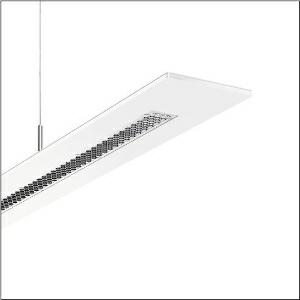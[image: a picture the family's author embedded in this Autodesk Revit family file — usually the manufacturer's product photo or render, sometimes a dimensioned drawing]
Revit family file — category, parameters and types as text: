
# Revit family: arktika_r__21_5mb2512l30840_559e
name_source: partatom
category: Lighting Fixtures
units: mm (PartAtom-declared; Revit-internal decimal feet)

## family parameters
Cut with Voids When Loaded = No
Host = Face
Light Source = No
Part Type = Normal
Room Calculation Point = No
Round Connector Dimension = Use Diameter
Shared = No

## types (1)
- Arktika® 21 (1 x LED 4000K / CRI = 80 (unbekannt), 4000 lm, 4000K)
    Apparent Load = 31 VA
    CIE Flux Codes = 81 100 100 79 100
    Color Rendering = 80
    Color Temperature = 4000K
    Default Elevation = 1800 mm
    Description = Arktika® 21, office luminaire, primary anti-glare with honeycomb louvre, of plastic, aluminium vaporised, highly specular, light emission: direct/indirect distribution, primary light characteristic: symmetric, installation type: suspended mounting, LED, rated luminous flux: 4.000lm, luminous efficacy: 130lm/W, light colour: 840, colour temperature: 4000K, control gear: ON/OFF, with terminal, 3-pole, mains connection: 220..240V, AC, 50/60Hz, rated input power: 31W, housing, of aluminium, powder-coated, traffic white (RAL 9016), 1-length, length: 1.250mm, width: 120mm, height: 8mm, protection rating (complete): IP20, insulation class (complete): insulation class II (safety insulation), certification: CE, packaging unit: 1 piece
    Height = 8 mm  [stored 0.0262467 ft]
    Lamp = 1 x LED 4000K / CRI >= 80 (unbekannt)
    Lamp Light Flux = 4000 lm
    Lamp count = 1
    Length = 1250 mm
    Luminous efficacy = 130 lm/W
    Manufacturer = Siteco
    ModVariant = No
    Model = 5MB2512L30840
    Mounting Place = Ceiling
    Mounting Type = Pendant
    Number of Poles = 1
    OnlyDefault = Yes
    Power Factor = 1
    Product Name = Arktika® 21
    Product group = office luminaire | ceiling pendant
    ProductGroupID = 903
    Protection Class = Protection class II
    Protection Degree = IP 20
    RLX_Detail_Level = 1
    RLX_Emergency_Light_Flux = 0 lm
    RLX_Emergency_Type = 0
    RLX_Emergency_Type_DB = No
    RlxData = <blob elided: 36057 chars, md5=f004a287>
    Socket = socket
    Standby Power = 0 W
    System Light Flux = 4000 lm
    System Power = 31 W
    Type Comments = Product without accessories
    Type Image = l_1006128.jpg
    URL = http://relux.com
    VarID = ---
    Voltage = 0 V
    Weight = 0.00 kg
    Width = 120 mm

note: [stored X ft] marks values corroborated as IEEE doubles in the binary element streams (Revit-internal decimal feet)

## geometry (parser evidence)
native form markers: Blend x4, Sweep x12
no freeform markers — native parametric forms only
